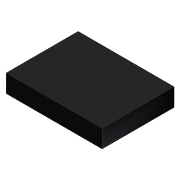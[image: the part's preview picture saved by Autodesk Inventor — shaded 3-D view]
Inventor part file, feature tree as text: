
AUTODESK INVENTOR PART (.ipt)
format: ipt  version: unknown  size: 165,888 bytes
history: native  units: mm
features: extrude x1, sketch x1
ambient origin geometry x8: Origin, YZ Plane, XZ Plane, XY Plane, X Axis, Y Axis, Z Axis, Center Point
feature tree (2):
  extrude  "Выдавливание2"  Depth=8.0mm
  sketch  "Эскиз2"
